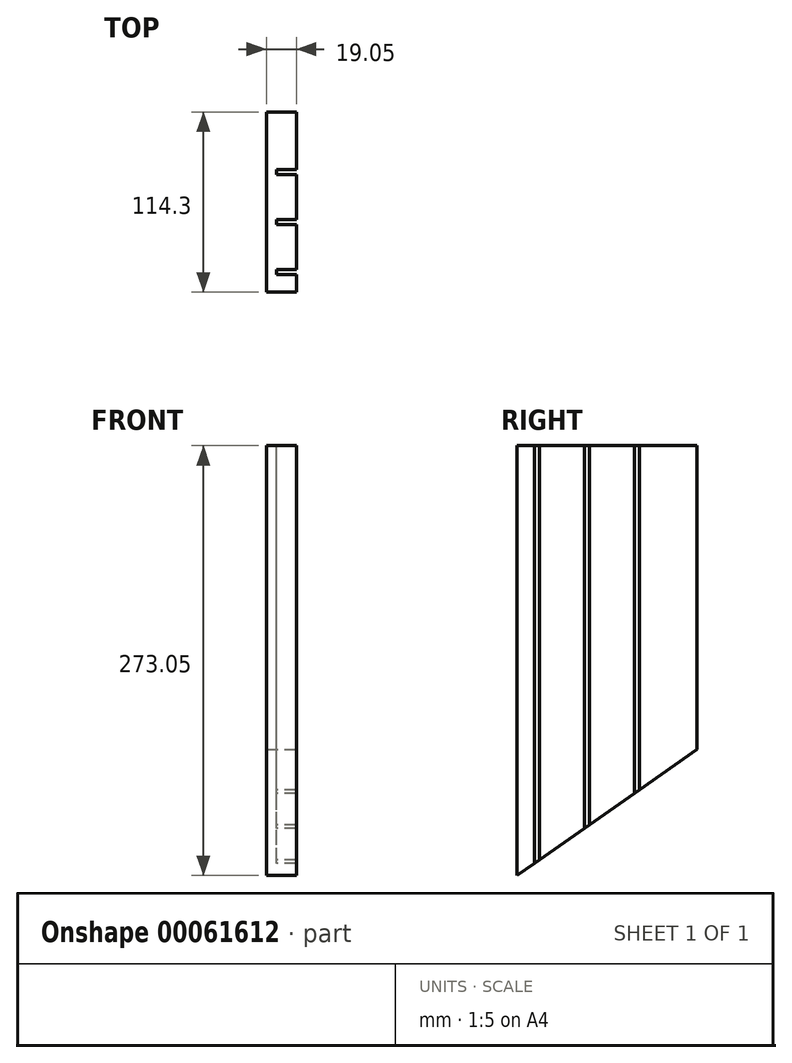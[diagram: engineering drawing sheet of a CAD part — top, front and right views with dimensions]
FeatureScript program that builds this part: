
annotation { "Feature Type Name" : "Feature", "Feature Type Description" : "" }
export const myFeature = defineFeature(function(context is Context, id is Id, definition is map)
    precondition{}
    {
        {
            var Q0;
            Q0=qCreatedBy(makeId("Right.planeOp"),FACE);
            var sketch = newSketch(context, id + "F0", { "sketchPlane" : qUnion([Q0])});
            skLineSegment(sketch, "E0.bottom", {"start": v(0, 0) * mm, "end": v(-114.3, 0) * mm});
            skLineSegment(sketch, "E0.top", {"start": v(0, -273.05) * mm, "end": v(-114.3, -273.05) * mm});
            skLineSegment(sketch, "E0.left", {"start": v(0, 0) * mm, "end": v(0, -273.05) * mm});
            skLineSegment(sketch, "E0.right", {"start": v(-114.3, 0) * mm, "end": v(-114.3, -273.05) * mm});
            skSolve(sketch);
        }
        {
            var Q0;
            Q0 = qSketchRegion(id + "F0", true);
            extrude(context, id + "F1", {"entities" : qUnion([Q0]), "depth" : 19.05 * mm});
        }
        {
            var Q0;
            Q0=makeQuery(id+"F1.opExtrude","CAP_FACE",FACE,{"disambiguationData":[OSD([sQuery(id+"F0.wireOp",EDGE,"E0.bottom"),sQuery(id+"F0.wireOp",EDGE,"E0.top"),sQuery(id+"F0.wireOp",EDGE,"E0.left"),sQuery(id+"F0.wireOp",EDGE,"E0.right")])],"isStart":false});
            var sketch = newSketch(context, id + "F2", { "sketchPlane" : qUnion([Q0])});
            skLineSegment(sketch, "E1.bottom", {"start": v(-36.51, -273.05) * mm, "end": v(-39.69, -273.05) * mm});
            skLineSegment(sketch, "E1.top", {"start": v(-36.51, 0) * mm, "end": v(-39.69, 0) * mm});
            skLineSegment(sketch, "E1.left", {"start": v(-36.51, -273.05) * mm, "end": v(-36.51, 0) * mm});
            skLineSegment(sketch, "E1.right", {"start": v(-39.69, -273.05) * mm, "end": v(-39.69, 0) * mm});
            skLineSegment(sketch, "E2.bottom", {"start": v(-68.26, -273.05) * mm, "end": v(-71.44, -273.05) * mm});
            skLineSegment(sketch, "E2.top", {"start": v(-68.26, 0) * mm, "end": v(-71.44, 0) * mm});
            skLineSegment(sketch, "E2.left", {"start": v(-68.26, -273.05) * mm, "end": v(-68.26, 0) * mm});
            skLineSegment(sketch, "E2.right", {"start": v(-71.44, -273.05) * mm, "end": v(-71.44, 0) * mm});
            skLineSegment(sketch, "E3.bottom", {"start": v(-100.01, -273.05) * mm, "end": v(-103.19, -273.05) * mm});
            skLineSegment(sketch, "E3.top", {"start": v(-100.01, 0) * mm, "end": v(-103.19, 0) * mm});
            skLineSegment(sketch, "E3.left", {"start": v(-100.01, -273.05) * mm, "end": v(-100.01, 0) * mm});
            skLineSegment(sketch, "E3.right", {"start": v(-103.19, -273.05) * mm, "end": v(-103.19, 0) * mm});
            skSolve(sketch);
        }
        {
            var Q0;
            Q0 = qSketchRegion(id + "F2", true);
            extrude(context, id + "F3", {"entities" : qUnion([Q0]), "operationType" : NewBodyOperationType.REMOVE, "oppositeDirection" : true, "depth" : 12.7 * mm});
        }
        {
            var Q0;
            {var subQ0=sQuery(id+"F0.wireOp",EDGE,"E0.right");var subQ1=sQuery(id+"F0.wireOp",EDGE,"E0.top");var subQ2=sQuery(id+"F0.wireOp",EDGE,"E0.bottom");Q0=makeQuery(id+"F3.boolean.opBoolean","SPLIT",FACE,{"disambiguationData":[TD([makeQuery(id+"F1.opExtrude","SWEPT_FACE",FACE,{"disambiguationData":[OSD([subQ0])]})])],"derivedFrom":makeQuery(id+"F1.opExtrude","CAP_FACE",FACE,{"disambiguationData":[OSD([subQ2,subQ1,sQuery(id+"F0.wireOp",EDGE,"E0.left"),subQ0])],"isStart":false})});}
            var sketch = newSketch(context, id + "F4", { "sketchPlane" : qUnion([Q0])});
            skLineSegment(sketch, "E4", {"start": v(-114.3, -273.05) * mm, "end": v(0, -193.02) * mm});
            skLineSegment(sketch, "E5", {"start": v(0, -193.02) * mm, "end": v(0, -273.05) * mm});
            skLineSegment(sketch, "E6", {"start": v(0, -273.05) * mm, "end": v(-114.3, -273.05) * mm});
            skSolve(sketch);
        }
        {
            var Q0;
            Q0 = qSketchRegion(id + "F4", true);
            extrude(context, id + "F5", {"entities" : qUnion([Q0]), "operationType" : NewBodyOperationType.REMOVE, "endBound" : BoundingType.THROUGH_ALL, "oppositeDirection" : true, "depth" : 25.4 * mm});
        }
    });
